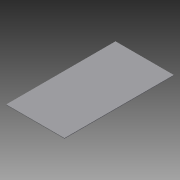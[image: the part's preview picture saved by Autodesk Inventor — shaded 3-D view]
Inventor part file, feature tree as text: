
AUTODESK INVENTOR PART (.ipt)
format: ipt  version: 2014 (Build 180170000, 170)  size: 67,584 bytes
history: native  units: in
note: dims shown in document units (in); Inventor stores cm internally (conversion verified against a paired STEP export)
features: extrude x1, sketch x1
ambient origin geometry x8: Origin, YZ Plane, XZ Plane, XY Plane, X Axis, Y Axis, Z Axis, Center Point
bodies: Solid1 (feature_tree)
feature tree (2):
  extrude  "Extrusion1"  Depth=12.341in
  sketch  "Sketch1"  dims[d0=6.582in d1=12.341in d2=0.0625in d3=0.0in]
